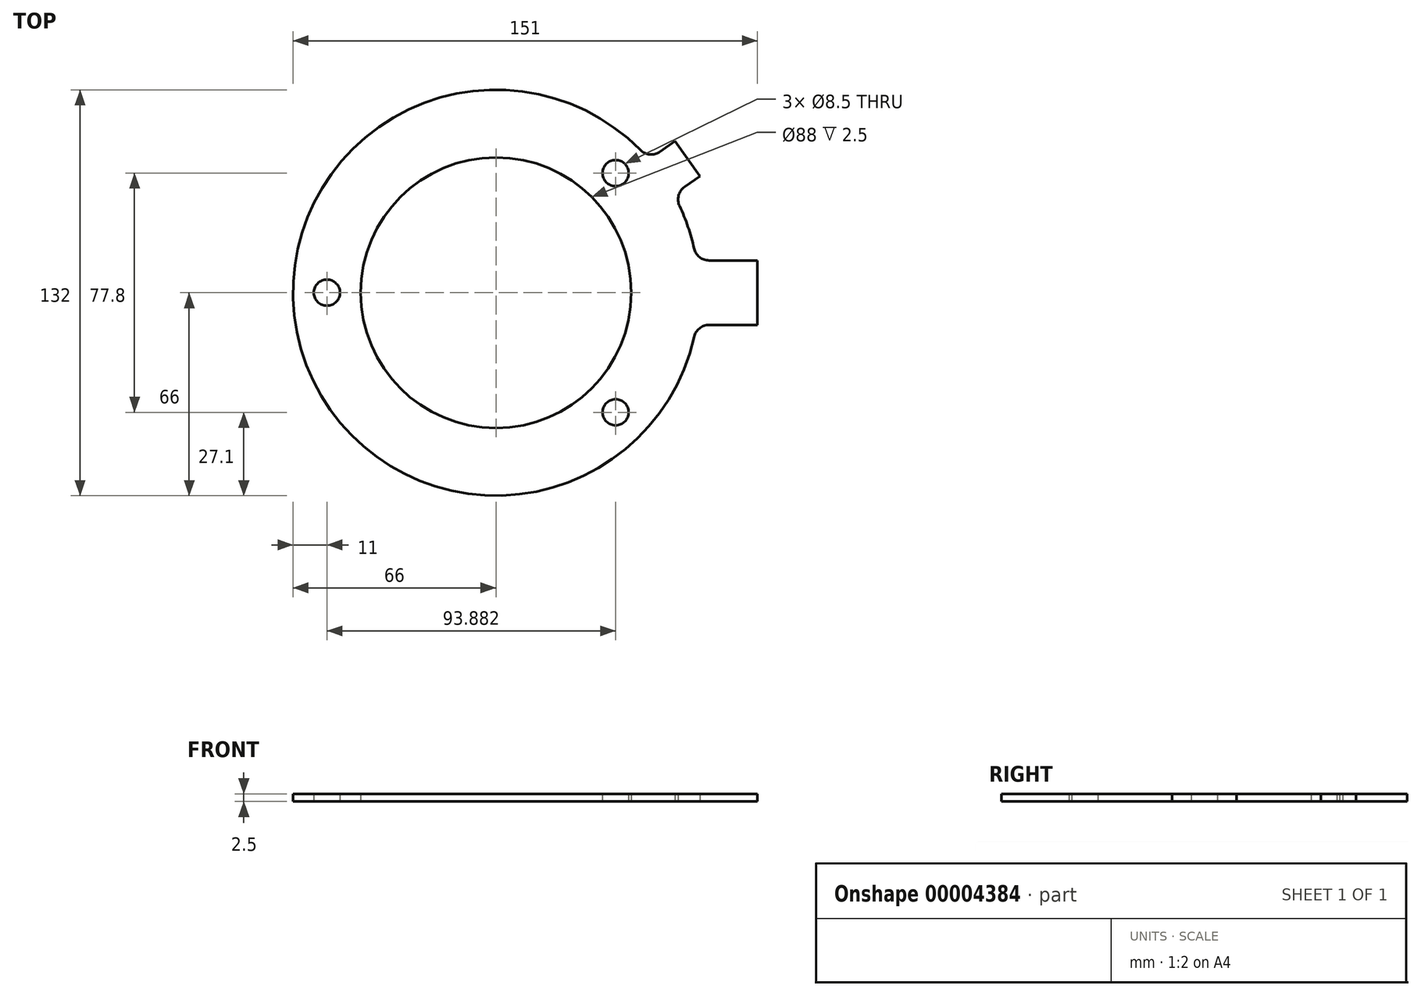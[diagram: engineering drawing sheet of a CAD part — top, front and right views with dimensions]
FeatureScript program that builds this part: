
annotation { "Feature Type Name" : "Feature", "Feature Type Description" : "" }
export const myFeature = defineFeature(function(context is Context, id is Id, definition is map)
    precondition{}
    {
        {
            var Q0;
            Q0=qCreatedBy(makeId("Top.planeOp"),FACE);
            var sketch = newSketch(context, id + "F0", { "sketchPlane" : qUnion([Q0])});
            skCircle(sketch, "E0", {"center": v(0, 0) * mm, "radius": 44 * mm});
            skArc(sketch, "E1", {"start": v(65.16, 10.5) * mm, "mid": v(62.4, 21.52) * mm, "end": v(57.77, 31.9) * mm});
            skLineSegment(sketch, "E2", {"start": v(65.16, 10.5) * mm, "end": v(85, 10.5) * mm});
            skLineSegment(sketch, "E3", {"start": v(85, -10.5) * mm, "end": v(65.16, -10.5) * mm});
            skCircle(sketch, "E4", {"center": v(-55, 0) * mm, "radius": 4.25 * mm});
            skCircle(sketch, "E5", {"center": v(38.88, 38.9) * mm, "radius": 4.25 * mm});
            skCircle(sketch, "E6", {"center": v(38.88, -38.9) * mm, "radius": 4.25 * mm});
            skLineSegment(sketch, "E7", {"start": v(85, 10.5) * mm, "end": v(85, -10.5) * mm});
            skLineSegment(sketch, "E8", {"start": v(0, 0) * mm, "end": v(62.26, 43.6) * mm, "construction": true});
            skLineSegment(sketch, "E9", {"start": v(49.74, 43.38) * mm, "end": v(58.24, 49.33) * mm});
            skLineSegment(sketch, "E10", {"start": v(57.77, 31.9) * mm, "end": v(66.27, 37.86) * mm});
            skLineSegment(sketch, "E11", {"start": v(58.24, 49.33) * mm, "end": v(66.27, 37.86) * mm});
            skPoint(sketch, "E12", {"position": v(49.74, 43.38) * mm});
            skPoint(sketch, "E13", {"position": v(57.77, 31.9) * mm});
            skArc(sketch, "E14.trimOffspring", {"start": v(49.74, 43.38) * mm, "mid": v(-63.45, -18.16) * mm, "end": v(65.16, -10.5) * mm});
            skSolve(sketch);
        }
        {
            var Q0;
            Q0 = qSketchRegion(id + "F0", true);
            extrude(context, id + "F1", {"entities" : qUnion([Q0]), "depth" : 2.5 * mm});
        }
        {
            var Q0;
            Q0=makeQuery(id+"F1.opExtrude","SWEPT_EDGE",EDGE,{"disambiguationData":[OSD([sQuery(id+"F0.wireOp",EDGE,"E1"),sQuery(id+"F0.wireOp",EDGE,"E10")])]});
            var Q1;
            Q1=makeQuery(id+"F1.opExtrude","SWEPT_EDGE",EDGE,{"disambiguationData":[OSD([sQuery(id+"F0.wireOp",EDGE,"E9"),sQuery(id+"F0.wireOp",EDGE,"E14.trimOffspring")])]});
            fillet(context, id + "F2", {"entities" : qUnion([Q0, Q1]), "radius" : 5 * mm, "tangentPropagation" : true, "allowEdgeOverflow" : false});
        }
        {
            var Q0;
            Q0=makeQuery(id+"F1.opExtrude","SWEPT_EDGE",EDGE,{"disambiguationData":[OSD([sQuery(id+"F0.wireOp",EDGE,"E3"),sQuery(id+"F0.wireOp",EDGE,"E14.trimOffspring")])]});
            var Q1;
            Q1=makeQuery(id+"F1.opExtrude","SWEPT_EDGE",EDGE,{"disambiguationData":[OSD([sQuery(id+"F0.wireOp",EDGE,"E1"),sQuery(id+"F0.wireOp",EDGE,"E2")])]});
            fillet(context, id + "F3", {"entities" : qUnion([Q0, Q1]), "radius" : 5 * mm, "tangentPropagation" : true, "allowEdgeOverflow" : false});
        }
    });
